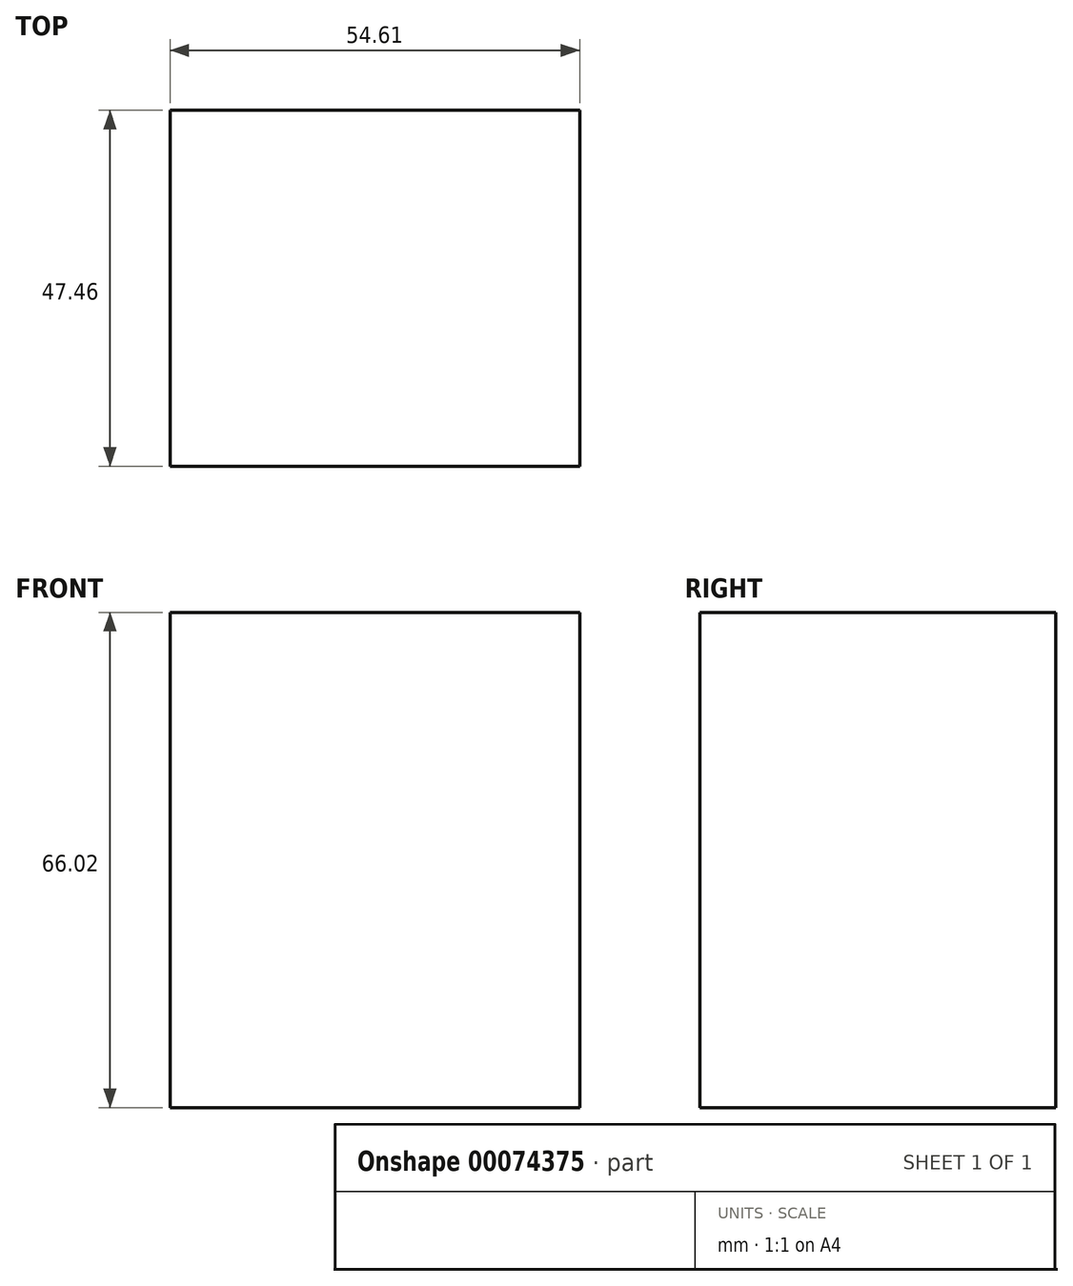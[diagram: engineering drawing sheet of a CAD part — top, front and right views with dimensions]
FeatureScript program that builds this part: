
annotation { "Feature Type Name" : "Feature", "Feature Type Description" : "" }
export const myFeature = defineFeature(function(context is Context, id is Id, definition is map)
    precondition{}
    {
        {
            var Q0;
            Q0=qCreatedBy(makeId("Top.planeOp"),FACE);
            var sketch = newSketch(context, id + "F0", { "sketchPlane" : qUnion([Q0])});
            skLineSegment(sketch, "E0.bottom", {"start": v(0, 0) * mm, "end": v(54.6, 0) * mm});
            skLineSegment(sketch, "E0.top", {"start": v(0, -47.46) * mm, "end": v(54.6, -47.46) * mm});
            skLineSegment(sketch, "E0.left", {"start": v(0, 0) * mm, "end": v(0, -47.46) * mm});
            skLineSegment(sketch, "E0.right", {"start": v(54.6, 0) * mm, "end": v(54.6, -47.46) * mm});
            skCircle(sketch, "E1", {"center": v(27.3, -23.73) * mm, "radius": 15.25 * mm});
            skPoint(sketch, "E1.centerSnap0", {"position": v(0, -23.73) * mm});
            skLineSegment(sketch, "E2", {"start": v(27.3, -23.73) * mm, "end": v(27.3, 0) * mm, "construction": true});
            skSolve(sketch);
        }
        {
            var Q0;
            Q0 = qSketchRegion(id + "F0", true);
            var Q1;
            Q1=makeQuery(id+"F0.imprint","IMPRINT",FACE,{"disambiguationData":[TD([[makeQuery(id+"F0.imprint","IMPRINT",EDGE,{"derivedFrom":sQuery(id+"F0.wireOp",EDGE,"E1")}),1.0]])]});
            extrude(context, id + "F1", {"entities" : qUnion([Q0, Q1]), "depth" : 40.62 * mm, "hasSecondDirection" : true, "secondDirectionOppositeDirection" : true, "secondDirectionDepth" : 25.4 * mm});
        }
    });
